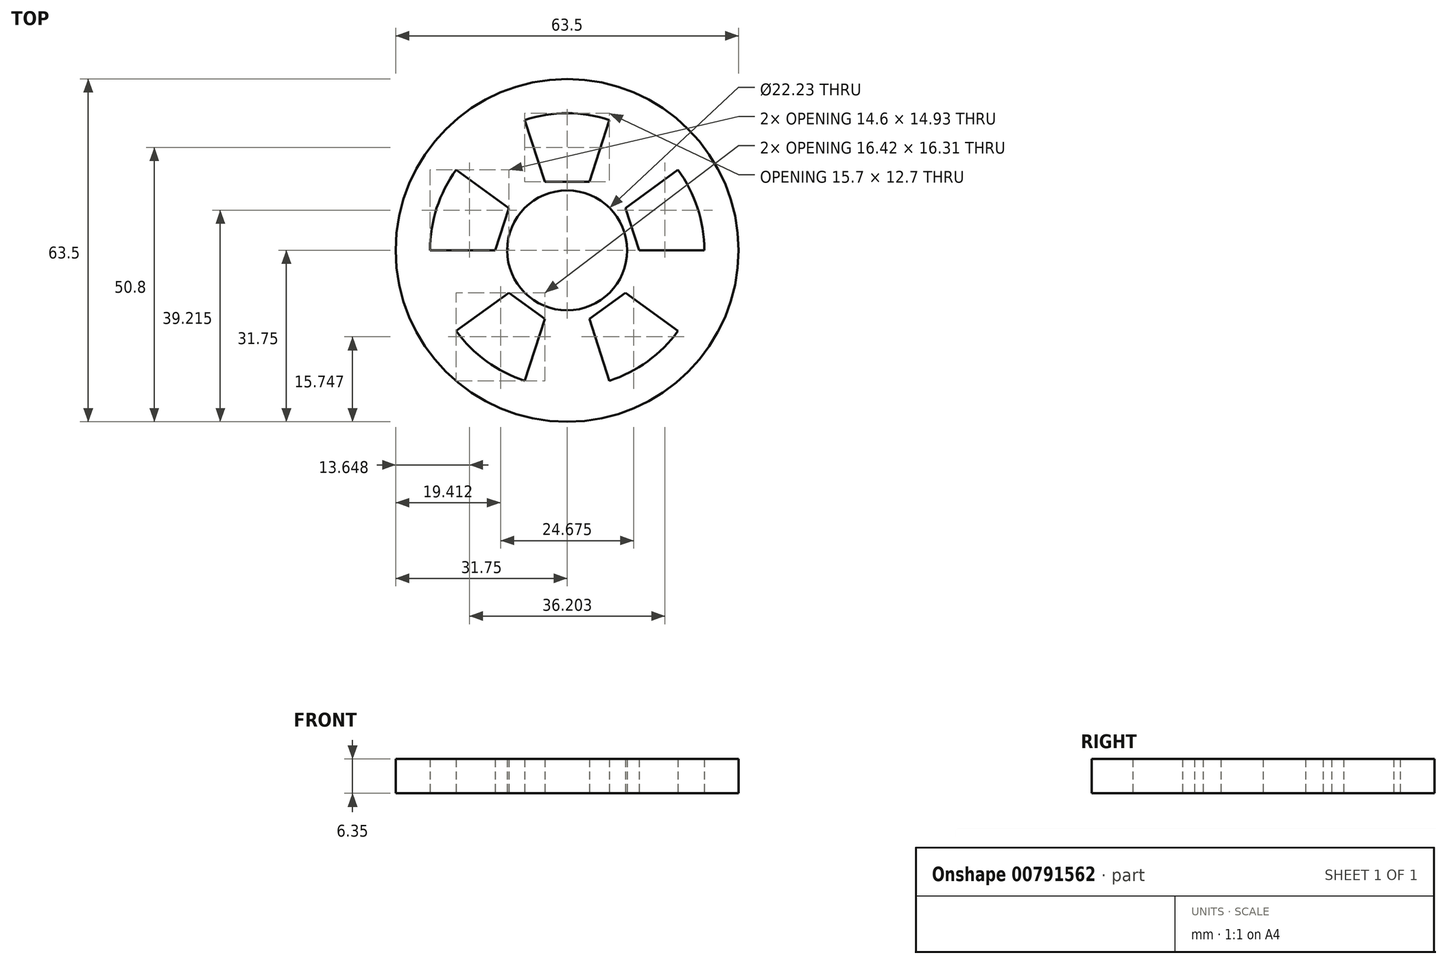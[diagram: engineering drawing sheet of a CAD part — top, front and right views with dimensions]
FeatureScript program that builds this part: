
annotation { "Feature Type Name" : "Feature", "Feature Type Description" : "" }
export const myFeature = defineFeature(function(context is Context, id is Id, definition is map)
    precondition{}
    {
        {
            var Q0;
            Q0=qCreatedBy(makeId("Top.planeOp"),FACE);
            var sketch = newSketch(context, id + "F0", { "sketchPlane" : qUnion([Q0])});
            skCircle(sketch, "E0.cCircle", {"center": v(0, 0) * mm, "radius": 12.7 * mm, "construction": true});
            skLineSegment(sketch, "E0.0", {"start": v(-4.13, 12.7) * mm, "end": v(4.13, 12.7) * mm});
            skLineSegment(sketch, "E0.1", {"start": v(4.13, 12.7) * mm, "end": v(10.8, 7.85) * mm});
            skLineSegment(sketch, "E0.2", {"start": v(10.8, 7.85) * mm, "end": v(13.35, 0) * mm});
            skLineSegment(sketch, "E0.3", {"start": v(13.35, 0) * mm, "end": v(10.8, -7.85) * mm});
            skLineSegment(sketch, "E0.4", {"start": v(10.8, -7.85) * mm, "end": v(4.13, -12.7) * mm});
            skLineSegment(sketch, "E0.5", {"start": v(4.13, -12.7) * mm, "end": v(-4.13, -12.7) * mm});
            skLineSegment(sketch, "E0.6", {"start": v(-4.13, -12.7) * mm, "end": v(-10.8, -7.85) * mm});
            skLineSegment(sketch, "E0.7", {"start": v(-10.8, -7.85) * mm, "end": v(-13.35, 0) * mm});
            skLineSegment(sketch, "E0.8", {"start": v(-13.35, 0) * mm, "end": v(-10.8, 7.85) * mm});
            skLineSegment(sketch, "E0.9", {"start": v(-10.8, 7.85) * mm, "end": v(-4.13, 12.7) * mm});
            skPoint(sketch, "E0.0.midPoint", {"position": v(0, 12.7) * mm});
            skCircle(sketch, "E1", {"center": v(0, 0) * mm, "radius": 11.11 * mm});
            skLineSegment(sketch, "E2", {"start": v(-4.13, 12.7) * mm, "end": v(0, 0) * mm});
            skLineSegment(sketch, "E3", {"start": v(4.13, 12.7) * mm, "end": v(0, 0) * mm});
            skLineSegment(sketch, "E4", {"start": v(10.8, 7.85) * mm, "end": v(0, 0) * mm});
            skLineSegment(sketch, "E5", {"start": v(13.35, 0) * mm, "end": v(0, 0) * mm});
            skLineSegment(sketch, "E6", {"start": v(10.8, -7.85) * mm, "end": v(0, 0) * mm});
            skLineSegment(sketch, "E7", {"start": v(4.13, -12.7) * mm, "end": v(0, 0) * mm});
            skLineSegment(sketch, "E8", {"start": v(-4.13, -12.7) * mm, "end": v(0, 0) * mm});
            skLineSegment(sketch, "E9", {"start": v(-10.8, -7.85) * mm, "end": v(0, 0) * mm});
            skLineSegment(sketch, "E10", {"start": v(-13.35, 0) * mm, "end": v(0, 0) * mm});
            skLineSegment(sketch, "E11", {"start": v(-10.8, 7.85) * mm, "end": v(0, 0) * mm});
            skLineSegment(sketch, "E12", {"start": v(0, 0) * mm, "end": v(-7.85, 24.16) * mm});
            skLineSegment(sketch, "E13", {"start": v(0, 0) * mm, "end": v(7.85, 24.16) * mm});
            skArc(sketch, "E14", {"start": v(-7.85, 24.16) * mm, "mid": v(0, 25.4) * mm, "end": v(7.85, 24.16) * mm});
            skLineSegment(sketch, "E15.1.0", {"start": v(0, 0) * mm, "end": v(-25.4, 0) * mm});
            skLineSegment(sketch, "E15.1.1", {"start": v(0, 0) * mm, "end": v(-20.55, 14.93) * mm});
            skArc(sketch, "E15.1.2", {"start": v(-25.4, 0) * mm, "mid": v(-24.16, 7.85) * mm, "end": v(-20.55, 14.93) * mm});
            skLineSegment(sketch, "E15.2.0", {"start": v(0, 0) * mm, "end": v(-7.85, -24.16) * mm});
            skLineSegment(sketch, "E15.2.1", {"start": v(0, 0) * mm, "end": v(-20.55, -14.93) * mm});
            skArc(sketch, "E15.2.2", {"start": v(-7.85, -24.16) * mm, "mid": v(-14.93, -20.55) * mm, "end": v(-20.55, -14.93) * mm});
            skLineSegment(sketch, "E15.3.0", {"start": v(0, 0) * mm, "end": v(20.55, -14.93) * mm});
            skLineSegment(sketch, "E15.3.1", {"start": v(0, 0) * mm, "end": v(7.85, -24.16) * mm});
            skArc(sketch, "E15.3.2", {"start": v(20.55, -14.93) * mm, "mid": v(14.93, -20.55) * mm, "end": v(7.85, -24.16) * mm});
            skLineSegment(sketch, "E15.4.0", {"start": v(0, 0) * mm, "end": v(20.55, 14.93) * mm});
            skLineSegment(sketch, "E15.4.1", {"start": v(0, 0) * mm, "end": v(25.4, 0) * mm});
            skArc(sketch, "E15.4.2", {"start": v(20.55, 14.93) * mm, "mid": v(24.16, 7.85) * mm, "end": v(25.4, 0) * mm});
            skCircle(sketch, "E16", {"center": v(0, 0) * mm, "radius": 31.75 * mm});
            skSolve(sketch);
        }
        {
            var Q0;
            Q0 = qSketchRegion(id + "F0", true);
            var Q1;
            {var subQ0=sQuery(id+"F0.wireOp",EDGE,"E0.0");Q1=makeQuery(id+"F0.imprint","IMPRINT",FACE,{"disambiguationData":[TD([[makeQuery(id+"F0.imprint","IMPRINT",EDGE,{"derivedFrom":subQ0}),-1.0]])]});}
            var Q2;
            {var subQ0=sQuery(id+"F0.wireOp",EDGE,"E0.1");Q2=makeQuery(id+"F0.imprint","IMPRINT",FACE,{"disambiguationData":[TD([[makeQuery(id+"F0.imprint","IMPRINT",EDGE,{"derivedFrom":subQ0}),-1.0]])]});}
            var Q3;
            {var subQ0=sQuery(id+"F0.wireOp",EDGE,"E0.2");Q3=makeQuery(id+"F0.imprint","IMPRINT",FACE,{"disambiguationData":[TD([[makeQuery(id+"F0.imprint","IMPRINT",EDGE,{"derivedFrom":subQ0}),-1.0]])]});}
            var Q4;
            {var subQ0=sQuery(id+"F0.wireOp",EDGE,"E0.3");Q4=makeQuery(id+"F0.imprint","IMPRINT",FACE,{"disambiguationData":[TD([[makeQuery(id+"F0.imprint","IMPRINT",EDGE,{"derivedFrom":subQ0}),-1.0]])]});}
            var Q5;
            {var subQ0=sQuery(id+"F0.wireOp",EDGE,"E0.4");Q5=makeQuery(id+"F0.imprint","IMPRINT",FACE,{"disambiguationData":[TD([[makeQuery(id+"F0.imprint","IMPRINT",EDGE,{"derivedFrom":subQ0}),-1.0]])]});}
            var Q6;
            {var subQ0=sQuery(id+"F0.wireOp",EDGE,"E0.5");Q6=makeQuery(id+"F0.imprint","IMPRINT",FACE,{"disambiguationData":[TD([[makeQuery(id+"F0.imprint","IMPRINT",EDGE,{"derivedFrom":subQ0}),-1.0]])]});}
            var Q7;
            {var subQ0=sQuery(id+"F0.wireOp",EDGE,"E0.6");Q7=makeQuery(id+"F0.imprint","IMPRINT",FACE,{"disambiguationData":[TD([[makeQuery(id+"F0.imprint","IMPRINT",EDGE,{"derivedFrom":subQ0}),-1.0]])]});}
            var Q8;
            {var subQ0=sQuery(id+"F0.wireOp",EDGE,"E0.7");Q8=makeQuery(id+"F0.imprint","IMPRINT",FACE,{"disambiguationData":[TD([[makeQuery(id+"F0.imprint","IMPRINT",EDGE,{"derivedFrom":subQ0}),-1.0]])]});}
            var Q9;
            {var subQ0=sQuery(id+"F0.wireOp",EDGE,"E0.8");Q9=makeQuery(id+"F0.imprint","IMPRINT",FACE,{"disambiguationData":[TD([[makeQuery(id+"F0.imprint","IMPRINT",EDGE,{"derivedFrom":subQ0}),-1.0]])]});}
            var Q10;
            {var subQ0=sQuery(id+"F0.wireOp",EDGE,"E0.9");Q10=makeQuery(id+"F0.imprint","IMPRINT",FACE,{"disambiguationData":[TD([[makeQuery(id+"F0.imprint","IMPRINT",EDGE,{"derivedFrom":subQ0}),-1.0]])]});}
            extrude(context, id + "F1", {"entities" : qUnion([Q0, Q1, Q2, Q3, Q4, Q5, Q6, Q7, Q8, Q9, Q10]), "depth" : 6.35 * mm, "offsetDistance" : 25.4 * mm});
        }
    });
